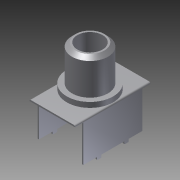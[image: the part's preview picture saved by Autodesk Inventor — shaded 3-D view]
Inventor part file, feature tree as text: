
AUTODESK INVENTOR PART (.ipt)
format: ipt  version: 2011 SP1 (Build 150282100, 282)  size: 182,784 bytes
history: native  units: in
note: dims shown in document units (in); Inventor stores cm internally (conversion verified against a paired STEP export)
features: other x35, sketch x5, extrude x3, revolve x1, hole x1
ambient origin geometry x8: Origin, YZ Plane, XZ Plane, XY Plane, X Axis, Y Axis, Z Axis, Center Point
bodies: Solid1 (feature_tree)
feature tree (45):
  extrude  "Extrusion1"  Depth=0.311in TaperAngle=0.0deg
  extrude  "Extrusion2"  Depth=0.308in TaperAngle=0.0deg
  revolve  "Revolution1"  [1 undecoded]
  extrude  "Extrusion3"  [1 undecoded]
  hole  "Drilling 1"  [1 undecoded]
  other  "1_XY"
  other  "1_YZ"
  other  "1_ZX"
  other  "1_X"
  other  "1_Y"
  other  "1_Z"
  other  "1_Center"
  other  "2_XY"
  other  "2_YZ"
  other  "2_ZX"
  other  "2_X"
  other  "2_Y"
  other  "2_Z"
  other  "2_Center"
  other  "3_XY"
  other  "3_YZ"
  other  "3_ZX"
  other  "3_X"
  other  "3_Y"
  other  "3_Z"
  other  "3_Center"
  other  "4_XY"
  other  "4_YZ"
  other  "4_ZX"
  other  "4_X"
  other  "4_Y"
  other  "4_Z"
  other  "4_Center"
  other  "to_base_XY"
  other  "to_base_YZ"
  other  "to_base_ZX"
  other  "to_base_X"
  other  "to_base_Y"
  other  "to_base_Z"
  other  "to_base_Center"
  sketch  "Sketch_1"  dims[d0=0.512in d1=0.0in d2=0.311in d3=0.0in]
  sketch  "Sketch_2"  dims[d4=360.0deg d5=0.308in d6=0.0in]
  sketch  "Sketch_7"
  sketch  "Sketch_8"
  sketch  "Sketch5"  dims[d7=0.1708in d8=0.75in d9=0.375in d10=0.25in d11=0.5635in d12=0.305in d13=0.0in]
note: 3 required parameter values undecoded (feature->parameter linkage not recoverable at this tier; creation-order binding heuristic only, values carry confidence <= 0.55)
